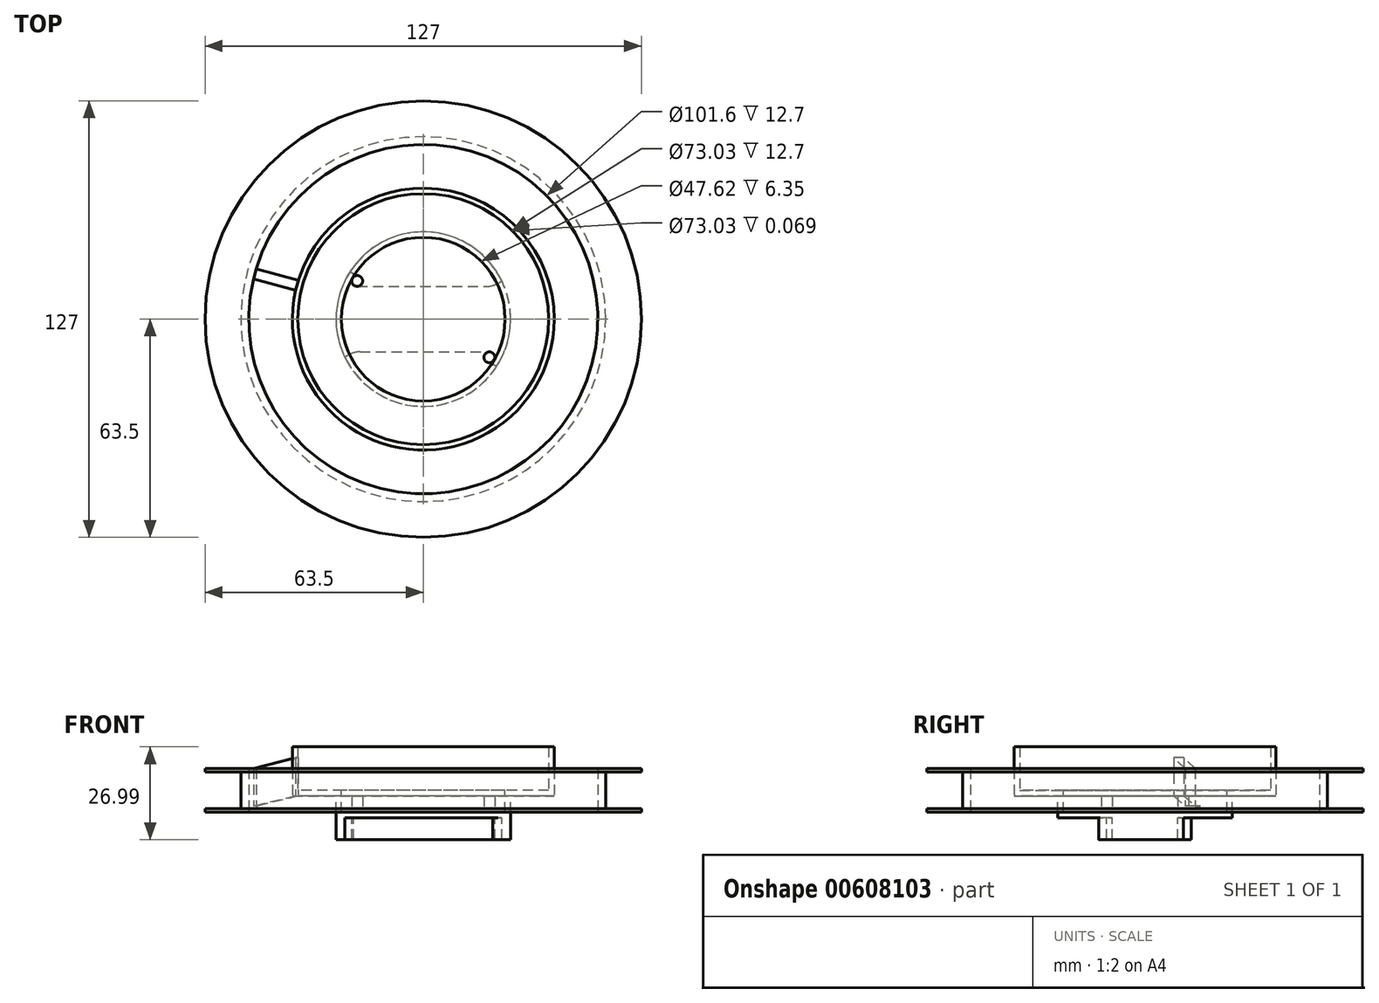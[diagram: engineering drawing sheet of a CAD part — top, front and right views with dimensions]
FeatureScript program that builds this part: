
annotation { "Feature Type Name" : "Feature", "Feature Type Description" : "" }
export const myFeature = defineFeature(function(context is Context, id is Id, definition is map)
    precondition{}
    {
        {
            var Q0;
            Q0=qCreatedBy(makeId("Top.planeOp"),FACE);
            var sketch = newSketch(context, id + "F0", { "sketchPlane" : qUnion([Q0])});
            skCircle(sketch, "E0", {"center": v(0, 0) * mm, "radius": 63.5 * mm});
            skCircle(sketch, "E1", {"center": v(0, 0) * mm, "radius": 38.1 * mm});
            skCircle(sketch, "E2", {"center": v(0, 0) * mm, "radius": 25.4 * mm});
            skCircle(sketch, "E3", {"center": v(0, 0) * mm, "radius": 50.8 * mm});
            skCircle(sketch, "E4", {"center": v(0, 0) * mm, "radius": 36.51 * mm});
            skCircle(sketch, "E5", {"center": v(0, 0) * mm, "radius": 23.81 * mm});
            skSolve(sketch);
        }
        {
            var Q0;
            Q0=makeQuery(id+"F0.imprint","IMPRINT",FACE,{"disambiguationData":[TD([[makeQuery(id+"F0.imprint","IMPRINT",EDGE,{"derivedFrom":sQuery(id+"F0.wireOp",EDGE,"E0")}),1.0]])]});
            extrude(context, id + "F1", {"entities" : qUnion([Q0]), "endBound" : BoundingType.SYMMETRIC, "depth" : 12.7 * mm, "offsetDistance" : 25.4 * mm});
        }
        {
            var Q0;
            Q0=makeQuery(id+"F0.imprint","IMPRINT",FACE,{"disambiguationData":[TD([[makeQuery(id+"F0.imprint","IMPRINT",EDGE,{"derivedFrom":sQuery(id+"F0.wireOp",EDGE,"E1")}),1.0]])]});
            extrude(context, id + "F2", {"entities" : qUnion([Q0]), "operationType" : NewBodyOperationType.ADD, "depth" : 12.7 * mm, "offsetDistance" : 25.4 * mm});
        }
        {
            var Q0;
            Q0=makeQuery(id+"F0.imprint","IMPRINT",FACE,{"disambiguationData":[TD([[makeQuery(id+"F0.imprint","IMPRINT",EDGE,{"derivedFrom":sQuery(id+"F0.wireOp",EDGE,"E2")}),-1.0]])]});
            extrude(context, id + "F3", {"entities" : qUnion([Q0]), "oppositeDirection" : true, "depth" : 1.59 * mm, "offsetDistance" : 25.4 * mm});
        }
        {
            var Q0;
            Q0=makeQuery(id+"F0.imprint","IMPRINT",FACE,{"disambiguationData":[TD([[makeQuery(id+"F0.imprint","IMPRINT",EDGE,{"derivedFrom":sQuery(id+"F0.wireOp",EDGE,"E2")}),1.0]])]});
            extrude(context, id + "F4", {"entities" : qUnion([Q0]), "operationType" : NewBodyOperationType.ADD, "oppositeDirection" : true, "depth" : 6.35 * mm, "offsetDistance" : 25.4 * mm});
        }
        {
            var Q0;
            Q0=makeQuery(id+"F4.opExtrude","CAP_FACE",FACE,{"disambiguationData":[OSD([sQuery(id+"F0.wireOp",EDGE,"E2"),sQuery(id+"F0.wireOp",EDGE,"E5")])],"isStart":false});
            var sketch = newSketch(context, id + "F5", { "sketchPlane" : qUnion([Q0])});
            skCircle(sketch, "E6", {"center": v(0, 0) * mm, "radius": 25.4 * mm});
            skSolve(sketch);
        }
        {
            var Q0;
            Q0=qSketchRegion(id+"F5",true);
            extrude(context, id + "F6", {"entities" : qUnion([Q0]), "operationType" : NewBodyOperationType.ADD, "depth" : 1.59 * mm, "offsetDistance" : 25.4 * mm});
        }
        {
            var Q0;
            Q0=makeQuery(id+"F6.opExtrude","CAP_FACE",FACE,{"disambiguationData":[OSD([sQuery(id+"F5.wireOp",EDGE,"E6")])],"isStart":false});
            var sketch = newSketch(context, id + "F7", { "sketchPlane" : qUnion([Q0])});
            skLineSegment(sketch, "E7.bottom", {"start": v(-19.25, -9.53) * mm, "end": v(18.46, -9.53) * mm});
            skLineSegment(sketch, "E7.top", {"start": v(-18.46, 9.53) * mm, "end": v(19.25, 9.53) * mm});
            skLineSegment(sketch, "E7.right", {"start": v(23.55, -9.53) * mm, "end": v(23.55, 0) * mm});
            skPoint(sketch, "E7.middle", {"position": v(0, 0) * mm});
            skArc(sketch, "E8", {"start": v(-23.55, 9.52) * mm, "mid": v(-25.4, 0) * mm, "end": v(-23.55, -9.52) * mm});
            skArc(sketch, "E9", {"start": v(-19.25, -9.53) * mm, "mid": v(-20.69, -10.45) * mm, "end": v(-20.45, -12.15) * mm, "construction": true});
            skArc(sketch, "E10", {"start": v(-21.77, -13.1) * mm, "mid": v(-20.6, -13.33) * mm, "end": v(-20.45, -12.15) * mm});
            skArc(sketch, "E11", {"start": v(-23.55, -9.53) * mm, "mid": v(-22.73, -11.34) * mm, "end": v(-21.77, -13.1) * mm});
            skLineSegment(sketch, "E12", {"start": v(0, 0) * mm, "end": v(63.6, 0) * mm, "construction": true});
            skLineSegment(sketch, "E13", {"start": v(0, 0) * mm, "end": v(31.65, -54.81) * mm, "construction": true});
            skArc(sketch, "E14.MirrorC", {"start": v(20.45, 12.15) * mm, "mid": v(20.69, 10.45) * mm, "end": v(19.25, 9.53) * mm, "construction": true});
            skArc(sketch, "E15", {"start": v(23.55, -9.53) * mm, "mid": v(25.4, 0) * mm, "end": v(23.55, 9.52) * mm});
            skArc(sketch, "E16", {"start": v(-19.25, -9.53) * mm, "mid": v(-20.69, -10.45) * mm, "end": v(-20.45, -12.15) * mm});
            skArc(sketch, "E17", {"start": v(21.77, 13.1) * mm, "mid": v(20.6, 13.33) * mm, "end": v(20.45, 12.15) * mm});
            skArc(sketch, "E18", {"start": v(23.55, 9.53) * mm, "mid": v(22.73, 11.34) * mm, "end": v(21.77, 13.1) * mm});
            skArc(sketch, "E19", {"start": v(19.25, 9.53) * mm, "mid": v(20.69, 10.45) * mm, "end": v(20.45, 12.15) * mm});
            skLineSegment(sketch, "E20", {"start": v(21.97, -10.58) * mm, "end": v(22.82, -11.15) * mm});
            skLineSegment(sketch, "E21", {"start": v(-21.97, 10.58) * mm, "end": v(-22.82, 11.15) * mm});
            skArc(sketch, "E22", {"start": v(22.82, -11.15) * mm, "mid": v(23.2, -10.34) * mm, "end": v(23.55, -9.52) * mm});
            skArc(sketch, "E23", {"start": v(-22.82, 11.15) * mm, "mid": v(-23.2, 10.34) * mm, "end": v(-23.55, 9.53) * mm});
            skPoint(sketch, "E24.visualSharp", {"position": v(-20.37, 9.53) * mm});
            skArc(sketch, "E24.filletArc", {"start": v(-21.97, 10.58) * mm, "mid": v(-20.3, 9.8) * mm, "end": v(-18.46, 9.53) * mm});
            skPoint(sketch, "E25.visualSharp", {"position": v(20.37, -9.53) * mm});
            skArc(sketch, "E25.filletArc", {"start": v(21.97, -10.58) * mm, "mid": v(20.3, -9.8) * mm, "end": v(18.46, -9.53) * mm});
            skSolve(sketch);
        }
        {
            var Q0;
            Q0=qSketchRegion(id+"F7",true);
            extrude(context, id + "F8", {"entities" : qUnion([Q0]), "operationType" : NewBodyOperationType.ADD, "depth" : 6.35 * mm, "offsetDistance" : 25.4 * mm});
        }
        {
            var Q0;
            {var subQ0=sQuery(id+"F5.wireOp",EDGE,"E6");Q0=makeQuery(id+"F8.boolean.opBoolean","SPLIT",FACE,{"disambiguationData":[TD([makeQuery(id+"F8.opExtrude","SWEPT_FACE",FACE,{"disambiguationData":[OSD([sQuery(id+"F7.wireOp",EDGE,"E7.bottom")])]})])],"derivedFrom":makeQuery(id+"F6.opExtrude","CAP_FACE",FACE,{"disambiguationData":[OSD([subQ0])],"isStart":false})});}
            var sketch = newSketch(context, id + "F9", { "sketchPlane" : qUnion([Q0])});
            skCircle(sketch, "E26", {"center": v(-19.25, -11.11) * mm, "radius": 1.59 * mm});
            skCircle(sketch, "E27", {"center": v(19.25, 11.11) * mm, "radius": 1.59 * mm});
            skSolve(sketch);
        }
        {
            var Q0;
            {var subQ0=sQuery(id+"F9.wireOp",EDGE,"E26");var subQ1=makeQuery(id+"F9.imprint","INTERSECT",VERTEX,{"derivedFrom":[makeQuery(id+"F8.opExtrude","CAP_EDGE",EDGE,{"disambiguationData":[OSD([sQuery(id+"F7.wireOp",EDGE,"E7.bottom")])],"isStart":true}),subQ0]});Q0=makeQuery(id+"F9.imprint","IMPRINT",FACE,{"disambiguationData":[TD([[makeQuery(id+"F9.imprint","IMPRINT",EDGE,{"disambiguationData":[TD([[subQ1,-1.0]])],"derivedFrom":subQ0}),1.0]])]});}
            var Q1;
            Q1=makeQuery(id+"F9.imprint","IMPRINT",FACE,{"disambiguationData":[TD([[makeQuery(id+"F9.imprint","IMPRINT",EDGE,{"derivedFrom":sQuery(id+"F9.wireOp",EDGE,"E27")}),1.0]])]});
            var Q2;
            Q2=qConstructionFilter(qBodyType(qCreatedBy(id+"F9",EDGE),BodyType.WIRE),ConstructionObject.NO);
            extrude(context, id + "F10", {"entities" : qUnion([Q0, Q1]), "operationType" : NewBodyOperationType.ADD, "surfaceEntities" : qUnion([Q2]), "oppositeDirection" : true, "depth" : 6.35 * mm, "offsetDistance" : 25.4 * mm});
        }
        {
            var Q0;
            Q0=qCreatedBy(makeId("Front.planeOp"),FACE);
            var sketch = newSketch(context, id + "F11", { "sketchPlane" : qUnion([Q0])});
            skLineSegment(sketch, "E28", {"start": v(0, 0) * mm, "end": v(0, 12.7) * mm, "construction": true});
            skSolve(sketch);
        }
        {
            var Q0;
            Q0=qCreatedBy(makeId("Front.planeOp"),FACE);
            var sketch = newSketch(context, id + "F12", { "sketchPlane" : qUnion([Q0])});
            skLineSegment(sketch, "E29.bottom", {"start": v(64.34, -5.33) * mm, "end": v(53.1, -5.33) * mm});
            skLineSegment(sketch, "E29.top", {"start": v(64.34, 5.33) * mm, "end": v(53.1, 5.33) * mm});
            skLineSegment(sketch, "E29.right", {"start": v(53.1, -5.33) * mm, "end": v(53.1, 5.33) * mm});
            skLineSegment(sketch, "E30", {"start": v(64.34, 5.33) * mm, "end": v(64.34, -5.33) * mm});
            skSolve(sketch);
        }
        {
            var Q0;
            Q0=qSketchRegion(id+"F12",true);
            var Q1;
            Q1=sQuery(id+"F11.wireOp",EDGE,"E28");
            revolve(context, id + "F13", {"operationType" : NewBodyOperationType.REMOVE, "entities" : qUnion([Q0]), "axis" : qUnion([Q1]), "revolveType" : RevolveType.FULL, "oppositeDirection" : true});
        }
        {
            var Q0;
            Q0=makeQuery(id+"F0.imprint","IMPRINT",FACE,{"disambiguationData":[TD([[makeQuery(id+"F0.imprint","IMPRINT",EDGE,{"derivedFrom":sQuery(id+"F0.wireOp",EDGE,"E1")}),1.0]])]});
            extrude(context, id + "F14", {"entities" : qUnion([Q0]), "operationType" : NewBodyOperationType.ADD, "oppositeDirection" : true, "depth" : 1.66 * mm, "offsetDistance" : 25.4 * mm});
        }
        {
            var Q0;
            Q0=makeQuery(id+"F0.imprint","IMPRINT",FACE,{"disambiguationData":[TD([[makeQuery(id+"F0.imprint","IMPRINT",EDGE,{"derivedFrom":sQuery(id+"F0.wireOp",EDGE,"E1")}),-1.0]])]});
            var sketch = newSketch(context, id + "F15", { "sketchPlane" : qUnion([Q0])});
            skLineSegment(sketch, "E31", {"start": v(0, 0) * mm, "end": v(-38.1, 0) * mm, "construction": true});
            skLineSegment(sketch, "E32", {"start": v(0, -1.59) * mm, "end": v(0, 1.59) * mm});
            skLineSegment(sketch, "E33", {"start": v(0, -1.59) * mm, "end": v(-5.92, 0) * mm});
            skLineSegment(sketch, "E34", {"start": v(-36.28, 11.3) * mm, "end": v(-48.65, 14.62) * mm});
            skArc(sketch, "E35", {"start": v(-48.65, 14.62) * mm, "mid": v(-49.07, 13.15) * mm, "end": v(-49.44, 11.66) * mm});
            skArc(sketch, "E36", {"start": v(-36.28, 11.3) * mm, "mid": v(-36.8, 9.86) * mm, "end": v(-37.08, 8.35) * mm});
            skLineSegment(sketch, "E37.trimOffspring", {"start": v(-37.08, 8.35) * mm, "end": v(-49.44, 11.66) * mm});
            skSolve(sketch);
        }
        {
            var Q0;
            {var subQ4=sQuery(id+"F15.wireOp",EDGE,"E35");Q0=makeQuery(id+"F15.imprint","IMPRINT",FACE,{"disambiguationData":[TD([[makeQuery(id+"F15.imprint","IMPRINT",EDGE,{"derivedFrom":subQ4}),1.0]])]});}
            extrude(context, id + "F16", {"entities" : qUnion([Q0]), "operationType" : NewBodyOperationType.ADD, "depth" : 9.52 * mm, "offsetDistance" : 25.4 * mm, "hasSecondDirection" : true, "secondDirectionOppositeDirection" : true, "secondDirectionDepth" : 4.57 * mm});
        }
        {
            var Q0;
            Q0=makeQuery(id+"F16.opExtrude","SWEPT_FACE",FACE,{"disambiguationData":[OSD([sQuery(id+"F15.wireOp",EDGE,"E37.trimOffspring")])]});
            cPlane(context, id + "F17", {"entities" : qUnion([Q0]), "cplaneType" : CPlaneType.OFFSET, "offset" : 0 * mm, "width" : 152.4 * mm, "height" : 152.4 * mm});
        }
        {
            var Q0;
            Q0=qCreatedBy(id+"F17.planeOp",FACE);
            var sketch = newSketch(context, id + "F18", { "sketchPlane" : qUnion([Q0])});
            skLineSegment(sketch, "E38", {"start": v(-38.07, -1.66) * mm, "end": v(-50.78, -4.57) * mm});
            skLineSegment(sketch, "E39", {"start": v(-50.78, -4.57) * mm, "end": v(-38.07, -4.57) * mm});
            skLineSegment(sketch, "E40", {"start": v(-38.07, -4.57) * mm, "end": v(-38.07, -1.66) * mm});
            skLineSegment(sketch, "E41", {"start": v(-50.78, 6.35) * mm, "end": v(-38.07, 9.53) * mm});
            skLineSegment(sketch, "E42", {"start": v(-38.07, 9.53) * mm, "end": v(-50.78, 9.53) * mm});
            skLineSegment(sketch, "E43", {"start": v(-50.78, 6.35) * mm, "end": v(-50.8, 6.35) * mm});
            skLineSegment(sketch, "E44", {"start": v(-50.8, 6.35) * mm, "end": v(-52.56, 9.52) * mm});
            skLineSegment(sketch, "E45", {"start": v(-52.56, 9.52) * mm, "end": v(-50.78, 9.53) * mm});
            skSolve(sketch);
        }
        {
            var Q0;
            Q0=qSketchRegion(id+"F18",true);
            extrude(context, id + "F19", {"entities" : qUnion([Q0]), "operationType" : NewBodyOperationType.REMOVE, "oppositeDirection" : true, "depth" : 4.62 * mm, "offsetDistance" : 25.4 * mm});
        }
    });
